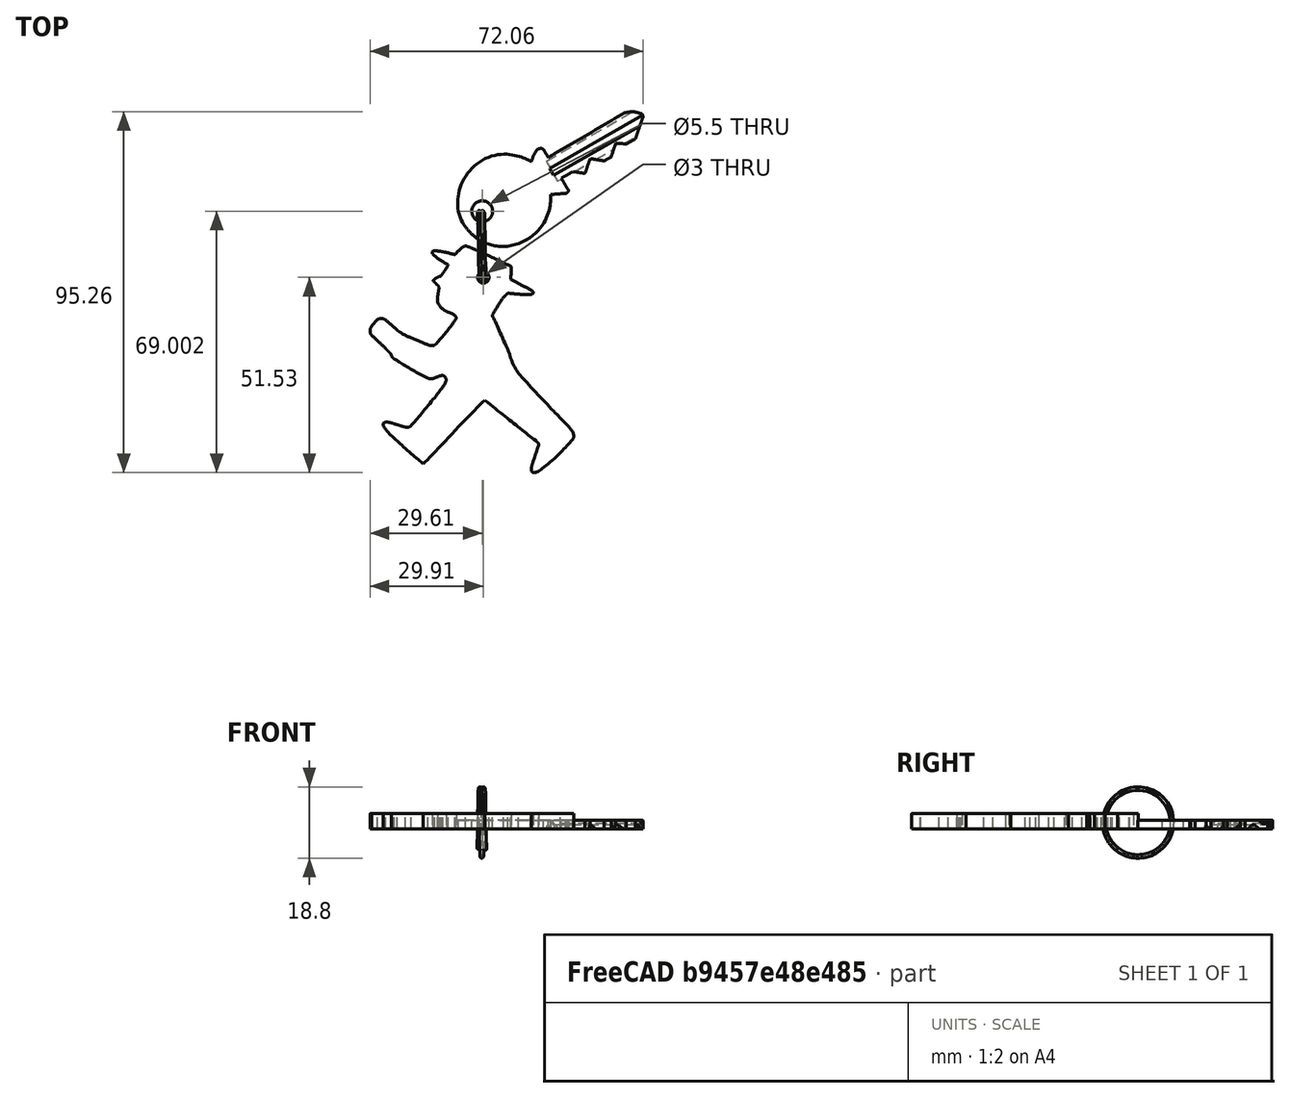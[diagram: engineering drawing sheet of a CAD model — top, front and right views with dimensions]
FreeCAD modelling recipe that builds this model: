
FCSTD DOCUMENT  (FreeCAD 0.18.4R)
Label: clauer_berlin_peaton
License: CreativeCommons Attribution-NonCommercial-ShareAlike
LicenseURL: http://creativecommons.org/licenses/by-nc-sa/4.0/
objects: Part::Feature×3, Part::Extrusion×1, Part::Cylinder×1, Part::Cut×1
note: 6 computed .brp shape members not serialized (recipe doc carries the construction recipe); baked Part::Feature solids carry a one-line shape summary decoded from their .brp

FEATURE [Part::Feature] path881
  shape: bbox 54.25 x 60.39 x 2e-07 mm, 0 faces, 0 solids (baked)
FEATURE [Part::Extrusion] Extrude
  Base = -> path881
  Dir = (0,0,1)
  DirMode = 2
  FaceMakerClass = Part::FaceMakerBullseye
  LengthFwd = 4
  LengthRev = 0
  Solid = true
  Symmetric = false
FEATURE [Part::Cylinder] Cylinder  label="Cilindre"
  Angle = 360
  AttacherType = Attacher::AttachEngine3D
  Height = 10
  Placement = pos=(2,3,-3) rot=(0,0,1;0rad)
  Radius = 1.5
FEATURE [Part::Cut] Cut  label="berlin_peaton"
  Base = -> Extrude
  Placement = pos=(-2,19,0) rot=(0,0,1;0rad)
  Refine = true
  Tool = -> Cylinder
FEATURE [Part::Feature] Cut001  label="key-model-1"
  Placement = pos=(-5.46976,36.5266,0) rot=(0,0,1;0.517888rad)
  shape: bbox 49.82 x 36.6 x 2.3 mm, 44 faces (baked)
FEATURE [Part::Feature] Sweep  label="key-ring-model-1"
  Placement = pos=(-1.2,30.2546,1.6391) rot=(0.333333,0.881918,0.333333;1.69612rad)
  shape: bbox 3.31 x 27.02 x 26.33 mm, 4 faces (baked)
